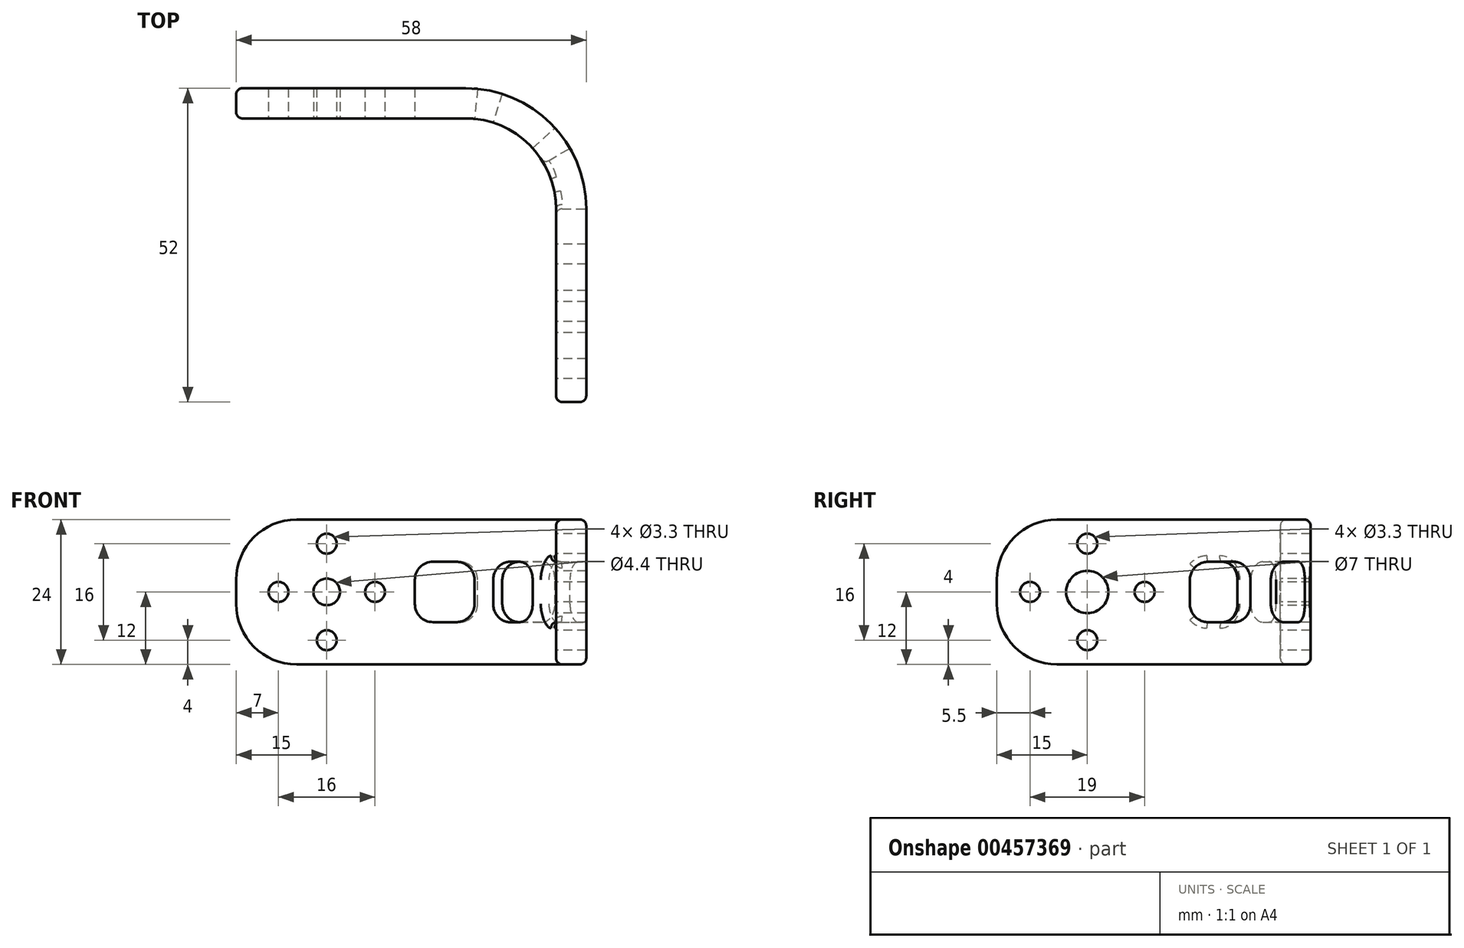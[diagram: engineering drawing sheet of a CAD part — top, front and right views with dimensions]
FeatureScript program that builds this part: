
annotation { "Feature Type Name" : "Feature", "Feature Type Description" : "" }
export const myFeature = defineFeature(function(context is Context, id is Id, definition is map)
    precondition{}
    {
        {
            var Q0;
            Q0=qCreatedBy(makeId("Top.planeOp"),FACE);
            var sketch = newSketch(context, id + "F0", { "sketchPlane" : qUnion([Q0])});
            skLineSegment(sketch, "E0", {"start": v(-15, 32) * mm, "end": v(23, 32) * mm});
            skLineSegment(sketch, "E1", {"start": v(38, 17) * mm, "end": v(38, -15) * mm});
            skLineSegment(sketch, "E2", {"start": v(38, -15) * mm, "end": v(43, -15) * mm});
            skLineSegment(sketch, "E3", {"start": v(43, -15) * mm, "end": v(43, 17) * mm});
            skLineSegment(sketch, "E4", {"start": v(23, 37) * mm, "end": v(-15, 37) * mm});
            skLineSegment(sketch, "E5", {"start": v(-15, 37) * mm, "end": v(-15, 32) * mm});
            skArc(sketch, "E6.filletArc", {"start": v(38, 17) * mm, "mid": v(33.6, 27.6) * mm, "end": v(23, 32) * mm});
            skArc(sketch, "E7.filletArc", {"start": v(43, 17) * mm, "mid": v(37.14, 31.14) * mm, "end": v(23, 37) * mm});
            skSolve(sketch);
        }
        {
            var Q0;
            Q0=qSketchRegion(id+"F0",true);
            extrude(context, id + "F1", {"entities" : qUnion([Q0]), "depth" : 12 * mm, "hasSecondDirection" : true, "secondDirectionOppositeDirection" : true, "secondDirectionDepth" : 12 * mm});
        }
        {
            var Q0;
            Q0=makeQuery(id+"F1.opExtrude","SWEPT_FACE",FACE,{"disambiguationData":[OSD([sQuery(id+"F0.wireOp",EDGE,"E1")])]});
            var sketch = newSketch(context, id + "F2", { "sketchPlane" : qUnion([Q0])});
            skCircle(sketch, "E8", {"center": v(0, 0) * mm, "radius": 17.4 * mm, "construction": true});
            skCircle(sketch, "E9", {"center": v(0, 0) * mm, "radius": 3.5 * mm});
            skCircle(sketch, "E10", {"center": v(0, 8) * mm, "radius": 1.65 * mm});
            skCircle(sketch, "E11.1.0", {"center": v(-9.5, 0) * mm, "radius": 1.65 * mm});
            skCircle(sketch, "E11.2.0", {"center": v(0, -8) * mm, "radius": 1.65 * mm});
            skCircle(sketch, "E11.3.0", {"center": v(9.5, 0) * mm, "radius": 1.65 * mm});
            skLineSegment(sketch, "E12", {"start": v(0, 18.26) * mm, "end": v(0, -16.55) * mm, "construction": true});
            skLineSegment(sketch, "E13", {"start": v(22.4, 0) * mm, "end": v(-24.3, 0) * mm, "construction": true});
            skPoint(sketch, "E13.endSnap0", {"position": v(-17, 0) * mm});
            skSolve(sketch);
        }
        {
            var Q0;
            Q0=qSketchRegion(id+"F2",true);
            extrude(context, id + "F3", {"entities" : qUnion([Q0]), "operationType" : NewBodyOperationType.REMOVE, "oppositeDirection" : true, "depth" : 5 * mm});
        }
        {
            var Q0;
            Q0=makeQuery(id+"F1.opExtrude","CAP_EDGE",EDGE,{"disambiguationData":[OSD([sQuery(id+"F0.wireOp",EDGE,"E5")])],"isStart":false});
            var Q1;
            Q1=makeQuery(id+"F1.opExtrude","CAP_EDGE",EDGE,{"disambiguationData":[OSD([sQuery(id+"F0.wireOp",EDGE,"E5")])],"isStart":true});
            var Q2;
            Q2=makeQuery(id+"F1.opExtrude","CAP_EDGE",EDGE,{"disambiguationData":[OSD([sQuery(id+"F0.wireOp",EDGE,"E2")])],"isStart":false});
            var Q3;
            Q3=makeQuery(id+"F1.opExtrude","CAP_EDGE",EDGE,{"disambiguationData":[OSD([sQuery(id+"F0.wireOp",EDGE,"E2")])],"isStart":true});
            fillet(context, id + "F4", {"entities" : qUnion([Q0, Q1, Q2, Q3]), "radius" : 10 * mm, "tangentPropagation" : true, "allowEdgeOverflow" : false});
        }
        {
            var Q0;
            Q0=makeQuery(id+"F1.opExtrude","CAP_VERTEX",VERTEX,{"disambiguationData":[OSD([sQuery(id+"F0.wireOp",EDGE,"E0"),sQuery(id+"F0.wireOp",EDGE,"E6.filletArc")])],"isStart":false});
            var Q1;
            {var subQ0=sQuery(id+"F0.wireOp",EDGE,"E5");Q1=makeQuery(id+"F4.opFillet","BLEND_VERTEX",VERTEX,{"blendedFrom":[makeQuery(id+"F1.opExtrude","CAP_EDGE",EDGE,{"disambiguationData":[OSD([subQ0])],"isStart":false}),makeQuery(id+"F1.opExtrude","SWEPT_FACE",FACE,{"disambiguationData":[OSD([sQuery(id+"F0.wireOp",EDGE,"E0")])]}),makeQuery(id+"F1.opExtrude","SWEPT_FACE",FACE,{"disambiguationData":[OSD([subQ0])]})],"blendedInto":[makeQuery(id+"F1.opExtrude","SWEPT_FACE",FACE,{"disambiguationData":[OSD([sQuery(id+"F0.wireOp",EDGE,"E0")])]}),makeQuery(id+"F1.opExtrude","SWEPT_FACE",FACE,{"disambiguationData":[OSD([subQ0])]})]});}
            var Q2;
            Q2=makeQuery(id+"F1.opExtrude","CAP_VERTEX",VERTEX,{"disambiguationData":[OSD([sQuery(id+"F0.wireOp",EDGE,"E0"),sQuery(id+"F0.wireOp",EDGE,"E6.filletArc")])],"isStart":true});
            cPlane(context, id + "F5", {"entities" : qUnion([Q0, Q1, Q2]), "cplaneType" : CPlaneType.THREE_POINT, "offset" : 150 * mm, "width" : 150 * mm, "height" : 150 * mm});
        }
        {
            var Q0;
            Q0=qCreatedBy(id+"F5.planeOp",FACE);
            var sketch = newSketch(context, id + "F6", { "sketchPlane" : qUnion([Q0])});
            skLineSegment(sketch, "E14", {"start": v(0, 21.33) * mm, "end": v(0, -20.01) * mm, "construction": true});
            skLineSegment(sketch, "E15", {"start": v(25.06, 0) * mm, "end": v(-19.8, 0) * mm, "construction": true});
            skCircle(sketch, "E16", {"center": v(0, 0) * mm, "radius": 17.4 * mm, "construction": true});
            skCircle(sketch, "E17", {"center": v(0, 0) * mm, "radius": 2.2 * mm});
            skCircle(sketch, "E18", {"center": v(0, 8) * mm, "radius": 1.65 * mm});
            skCircle(sketch, "E19.1.0", {"center": v(-8, 0) * mm, "radius": 1.65 * mm});
            skCircle(sketch, "E19.2.0", {"center": v(0, -8) * mm, "radius": 1.65 * mm});
            skCircle(sketch, "E19.3.0", {"center": v(8, 0) * mm, "radius": 1.65 * mm});
            skSolve(sketch);
        }
        {
            var Q0;
            Q0=qSketchRegion(id+"F6",true);
            extrude(context, id + "F7", {"entities" : qUnion([Q0]), "operationType" : NewBodyOperationType.REMOVE, "depth" : 5 * mm});
        }
        {
            var Q0;
            Q0=makeQuery(id+"F1.opExtrude","CAP_EDGE",EDGE,{"disambiguationData":[OSD([sQuery(id+"F0.wireOp",EDGE,"E0")])],"isStart":true});
            var Q1;
            Q1=makeQuery(id+"F1.opExtrude","CAP_EDGE",EDGE,{"disambiguationData":[OSD([sQuery(id+"F0.wireOp",EDGE,"E7.filletArc")])],"isStart":true});
            fillet(context, id + "F8", {"entities" : qUnion([Q0, Q1]), "radius" : 1 * mm, "tangentPropagation" : true, "allowEdgeOverflow" : false});
        }
        {
            var Q0;
            Q0=qCreatedBy(makeId("Top.planeOp"),FACE);
            var sketch = newSketch(context, id + "F9", { "sketchPlane" : qUnion([Q0])});
            skLineSegment(sketch, "E20", {"start": v(23, 37) * mm, "end": v(14.6, 37) * mm});
            skLineSegment(sketch, "E21", {"start": v(14.6, 37) * mm, "end": v(14.6, 32) * mm});
            skLineSegment(sketch, "E22", {"start": v(14.6, 32) * mm, "end": v(23, 32) * mm});
            skLineSegment(sketch, "E23", {"start": v(23, 17) * mm, "end": v(47.93, 17) * mm, "construction": true});
            skLineSegment(sketch, "E24", {"start": v(23, 17) * mm, "end": v(40.1, 32.46) * mm, "construction": true});
            skLineSegment(sketch, "E25", {"start": v(23, 17) * mm, "end": v(43.95, 29.16) * mm, "construction": true});
            skLineSegment(sketch, "E26", {"start": v(23, 17) * mm, "end": v(24.98, 36.77) * mm, "construction": true});
            skLineSegment(sketch, "E27", {"start": v(23, 17) * mm, "end": v(29.29, 36.67) * mm, "construction": true});
            skLineSegment(sketch, "E28", {"start": v(38, 17) * mm, "end": v(43, 17) * mm});
            skLineSegment(sketch, "E29", {"start": v(23, 17) * mm, "end": v(23, 38.2) * mm, "construction": true});
            skArc(sketch, "E30", {"start": v(43, 17) * mm, "mid": v(42.31, 22.2) * mm, "end": v(40.3, 27.04) * mm});
            skArc(sketch, "E31", {"start": v(38, 17) * mm, "mid": v(37.48, 20.9) * mm, "end": v(35.97, 24.53) * mm});
            skLineSegment(sketch, "E32", {"start": v(14.6, 37) * mm, "end": v(25, 36.9) * mm, "construction": true});
            skLineSegment(sketch, "E33", {"start": v(29.1, 36.05) * mm, "end": v(37.83, 30.42) * mm, "construction": true});
            skLineSegment(sketch, "E34", {"start": v(40.3, 27.04) * mm, "end": v(43, 17) * mm, "construction": true});
            skLineSegment(sketch, "E35", {"start": v(25, 36.9) * mm, "end": v(24.5, 31.93) * mm});
            skLineSegment(sketch, "E36", {"start": v(29.1, 36.05) * mm, "end": v(27.57, 31.29) * mm});
            skLineSegment(sketch, "E37", {"start": v(34.12, 27.06) * mm, "end": v(37.83, 30.42) * mm});
            skLineSegment(sketch, "E38", {"start": v(35.97, 24.53) * mm, "end": v(40.3, 27.04) * mm});
            skArc(sketch, "E39.trimOffspring", {"start": v(25, 36.9) * mm, "mid": v(24, 36.98) * mm, "end": v(23, 37) * mm});
            skArc(sketch, "E40.trimOffspring", {"start": v(24.5, 31.93) * mm, "mid": v(23.75, 31.98) * mm, "end": v(23, 32) * mm});
            skArc(sketch, "E41.trimOffspring", {"start": v(37.83, 30.42) * mm, "mid": v(33.83, 33.81) * mm, "end": v(29.1, 36.05) * mm});
            skArc(sketch, "E42.trimOffspring", {"start": v(34.12, 27.06) * mm, "mid": v(31.12, 29.6) * mm, "end": v(27.57, 31.29) * mm});
            skSolve(sketch);
        }
        {
            var Q0;
            Q0=qSketchRegion(id+"F9",true);
            extrude(context, id + "F10", {"entities" : qUnion([Q0]), "operationType" : NewBodyOperationType.REMOVE, "oppositeDirection" : true, "depth" : 5 * mm, "hasSecondDirection" : true, "secondDirectionOppositeDirection" : false, "secondDirectionDepth" : 5 * mm});
        }
        {
            var Q0;
            Q0=makeQuery(id+"F10.boolean.opBoolean","COPY",EDGE,{"derivedFrom":makeQuery(id+"F10.opExtrude","CAP_EDGE",EDGE,{"disambiguationData":[OSD([sQuery(id+"F9.wireOp",EDGE,"E21")])],"isStart":false})});
            var Q1;
            Q1=makeQuery(id+"F10.boolean.opBoolean","COPY",EDGE,{"derivedFrom":makeQuery(id+"F10.opExtrude","CAP_EDGE",EDGE,{"disambiguationData":[OSD([sQuery(id+"F9.wireOp",EDGE,"E35")])],"isStart":false})});
            var Q2;
            Q2=makeQuery(id+"F10.boolean.opBoolean","COPY",EDGE,{"derivedFrom":makeQuery(id+"F10.opExtrude","CAP_EDGE",EDGE,{"disambiguationData":[OSD([sQuery(id+"F9.wireOp",EDGE,"E36")])],"isStart":false})});
            var Q3;
            Q3=makeQuery(id+"F10.boolean.opBoolean","COPY",EDGE,{"derivedFrom":makeQuery(id+"F10.opExtrude","CAP_EDGE",EDGE,{"disambiguationData":[OSD([sQuery(id+"F9.wireOp",EDGE,"E21")])],"isStart":true})});
            var Q4;
            Q4=makeQuery(id+"F10.boolean.opBoolean","COPY",EDGE,{"derivedFrom":makeQuery(id+"F10.opExtrude","CAP_EDGE",EDGE,{"disambiguationData":[OSD([sQuery(id+"F9.wireOp",EDGE,"E35")])],"isStart":true})});
            var Q5;
            Q5=makeQuery(id+"F10.boolean.opBoolean","COPY",EDGE,{"derivedFrom":makeQuery(id+"F10.opExtrude","CAP_EDGE",EDGE,{"disambiguationData":[OSD([sQuery(id+"F9.wireOp",EDGE,"E36")])],"isStart":true})});
            var Q6;
            Q6=makeQuery(id+"F10.boolean.opBoolean","COPY",EDGE,{"derivedFrom":makeQuery(id+"F10.opExtrude","CAP_EDGE",EDGE,{"disambiguationData":[OSD([sQuery(id+"F9.wireOp",EDGE,"E37")])],"isStart":true})});
            var Q7;
            Q7=makeQuery(id+"F10.boolean.opBoolean","COPY",EDGE,{"derivedFrom":makeQuery(id+"F10.opExtrude","CAP_EDGE",EDGE,{"disambiguationData":[OSD([sQuery(id+"F9.wireOp",EDGE,"E37")])],"isStart":false})});
            var Q8;
            Q8=makeQuery(id+"F10.boolean.opBoolean","COPY",EDGE,{"derivedFrom":makeQuery(id+"F10.opExtrude","CAP_EDGE",EDGE,{"disambiguationData":[OSD([sQuery(id+"F9.wireOp",EDGE,"E38")])],"isStart":false})});
            var Q9;
            Q9=makeQuery(id+"F10.boolean.opBoolean","COPY",EDGE,{"derivedFrom":makeQuery(id+"F10.opExtrude","CAP_EDGE",EDGE,{"disambiguationData":[OSD([sQuery(id+"F9.wireOp",EDGE,"E38")])],"isStart":true})});
            var Q10;
            Q10=makeQuery(id+"F10.boolean.opBoolean","COPY",EDGE,{"derivedFrom":makeQuery(id+"F10.opExtrude","CAP_EDGE",EDGE,{"disambiguationData":[OSD([sQuery(id+"F9.wireOp",EDGE,"E28")])],"isStart":true})});
            var Q11;
            Q11=makeQuery(id+"F10.boolean.opBoolean","COPY",EDGE,{"derivedFrom":makeQuery(id+"F10.opExtrude","CAP_EDGE",EDGE,{"disambiguationData":[OSD([sQuery(id+"F9.wireOp",EDGE,"E28")])],"isStart":false})});
            fillet(context, id + "F11", {"entities" : qUnion([Q0, Q1, Q2, Q3, Q4, Q5, Q6, Q7, Q8, Q9, Q10, Q11]), "radius" : 3 * mm, "tangentPropagation" : true, "allowEdgeOverflow" : false});
        }
        {
            var Q0;
            Q0=makeQuery(id+"F10.boolean.opBoolean","COPY",EDGE,{"derivedFrom":makeQuery(id+"F10.opExtrude","CAP_EDGE",EDGE,{"disambiguationData":[OSD([sQuery(id+"F9.wireOp",EDGE,"E20")])],"isStart":false})});
            var Q1;
            Q1=makeQuery(id+"F10.boolean.opBoolean","COPY",EDGE,{"derivedFrom":makeQuery(id+"F10.opExtrude","CAP_EDGE",EDGE,{"disambiguationData":[OSD([sQuery(id+"F9.wireOp",EDGE,"E30")])],"isStart":false})});
            var Q2;
            Q2=makeQuery(id+"F10.boolean.opBoolean","COPY",EDGE,{"derivedFrom":makeQuery(id+"F10.opExtrude","CAP_EDGE",EDGE,{"disambiguationData":[OSD([sQuery(id+"F9.wireOp",EDGE,"E22")])],"isStart":false})});
            var Q3;
            Q3=makeQuery(id+"F10.boolean.opBoolean","COPY",EDGE,{"derivedFrom":makeQuery(id+"F10.opExtrude","CAP_EDGE",EDGE,{"disambiguationData":[OSD([sQuery(id+"F9.wireOp",EDGE,"E41.trimOffspring")])],"isStart":false})});
            var Q4;
            Q4=makeQuery(id+"F10.boolean.opBoolean","COPY",EDGE,{"derivedFrom":makeQuery(id+"F10.opExtrude","CAP_EDGE",EDGE,{"disambiguationData":[OSD([sQuery(id+"F9.wireOp",EDGE,"E42.trimOffspring")])],"isStart":false})});
            var Q5;
            Q5=makeQuery(id+"F10.boolean.opBoolean","MERGE",EDGE,{"derivedFrom":[makeQuery(id+"F1.opExtrude","SWEPT_EDGE",EDGE,{"disambiguationData":[OSD([sQuery(id+"F0.wireOp",EDGE,"E1"),sQuery(id+"F0.wireOp",EDGE,"E6.filletArc")])]}),makeQuery(id+"F10.opExtrude","SWEPT_EDGE",EDGE,{"disambiguationData":[OSD([sQuery(id+"F9.wireOp",EDGE,"E28"),sQuery(id+"F9.wireOp",EDGE,"E31")])]})]});
            fillet(context, id + "F12", {"entities" : qUnion([Q0, Q1, Q2, Q3, Q4, Q5]), "radius" : 1 * mm, "tangentPropagation" : true, "allowEdgeOverflow" : false});
        }
    });
